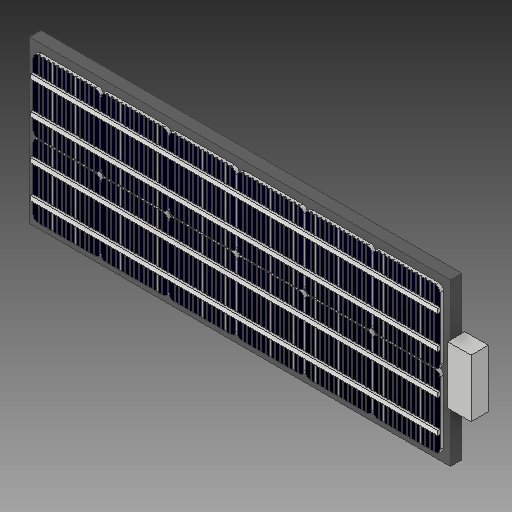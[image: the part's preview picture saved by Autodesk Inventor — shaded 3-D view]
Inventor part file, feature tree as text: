
AUTODESK INVENTOR PART (.ipt)
format: ipt  version: 2018 (Build 220112000, 112)  size: 736,768 bytes
history: native  units: in
note: dims shown in document units (in); Inventor stores cm internally (conversion verified against a paired STEP export)
features: sketch x7, extrude x6, pattern_linear x5
ambient origin geometry x8: Origin, YZ Plane, XZ Plane, XY Plane, X Axis, Y Axis, Z Axis, Center Point
bodies: Solid1 (feature_tree), Solid2 (feature_tree), Solid3 (feature_tree)
feature tree (18):
  extrude  "Extrusion1"  Depth=5.1181in
  extrude  "Extrusion2"  Depth=2.2835in
  pattern_linear  "Rectangular Pattern1"  Count1=6 Spacing1=2.3228in
  pattern_linear  "Rectangular Pattern2"  Count1=2 Spacing1=2.5in
  extrude  "Extrusion3"  Depth=4.9606in
  pattern_linear  "Rectangular Pattern3"  Spacing1=90.0deg  [1 undecoded]
  pattern_linear  "Rectangular Pattern4"  Spacing1=0.1772in  [1 undecoded]
  extrude  "Extrusion4"  Depth=4.9606in
  pattern_linear  "Rectangular Pattern5"  Spacing1=90.0deg  [1 undecoded]
  extrude  "Extrusion5"  Depth=0.0394in
  extrude  "Extrusion6"  Depth=0.0394in TaperAngle=0.0deg
  sketch  "Sketch7"  dims[d9=0.1181in d10=0.0in d11=2.3622in d13=2.3228in d14=0.7874in d16=2.5in d17=4.9606in d18=90.0deg d19=0.1772in d20=4.9606in d21=90.0deg d22=0.0394in d23=0.0394in d24=0.0in d25=5.1181in d27=0.1575in d28=2.3622in d30=2.3228in d31=13.8976in d32=0.1575in d33=0.5906in d34=0.7874in d36=1.122in d37=0.3937in d39=0.3937in d41=0.0787in d42=0.0in d43=0.7874in d45=2.4803in d46=0.1969in d47=0.3937in d48=0.0in d49=1.9685in d50=0.8019in d51=7.987in d52=0.9843in d53=0.5906in d54=0.0in]
  sketch  "Sketch1"  dims[d0=13.9764in d1=5.1181in]
  sketch  "Sketch2"  dims[d2=0.3937in d3=0.0in d4=2.2835in]
  sketch  "Sketch3"  dims[d5=2.4606in]
  sketch  "Sketch4"  dims[d6=0.0787in]
  sketch  "Sketch5"  dims[d7=0.0394in]
  sketch  "Sketch6"  dims[d8=0.1575in]
note: 3 required parameter values undecoded (feature->parameter linkage not recoverable at this tier; creation-order binding heuristic only, values carry confidence <= 0.55)
